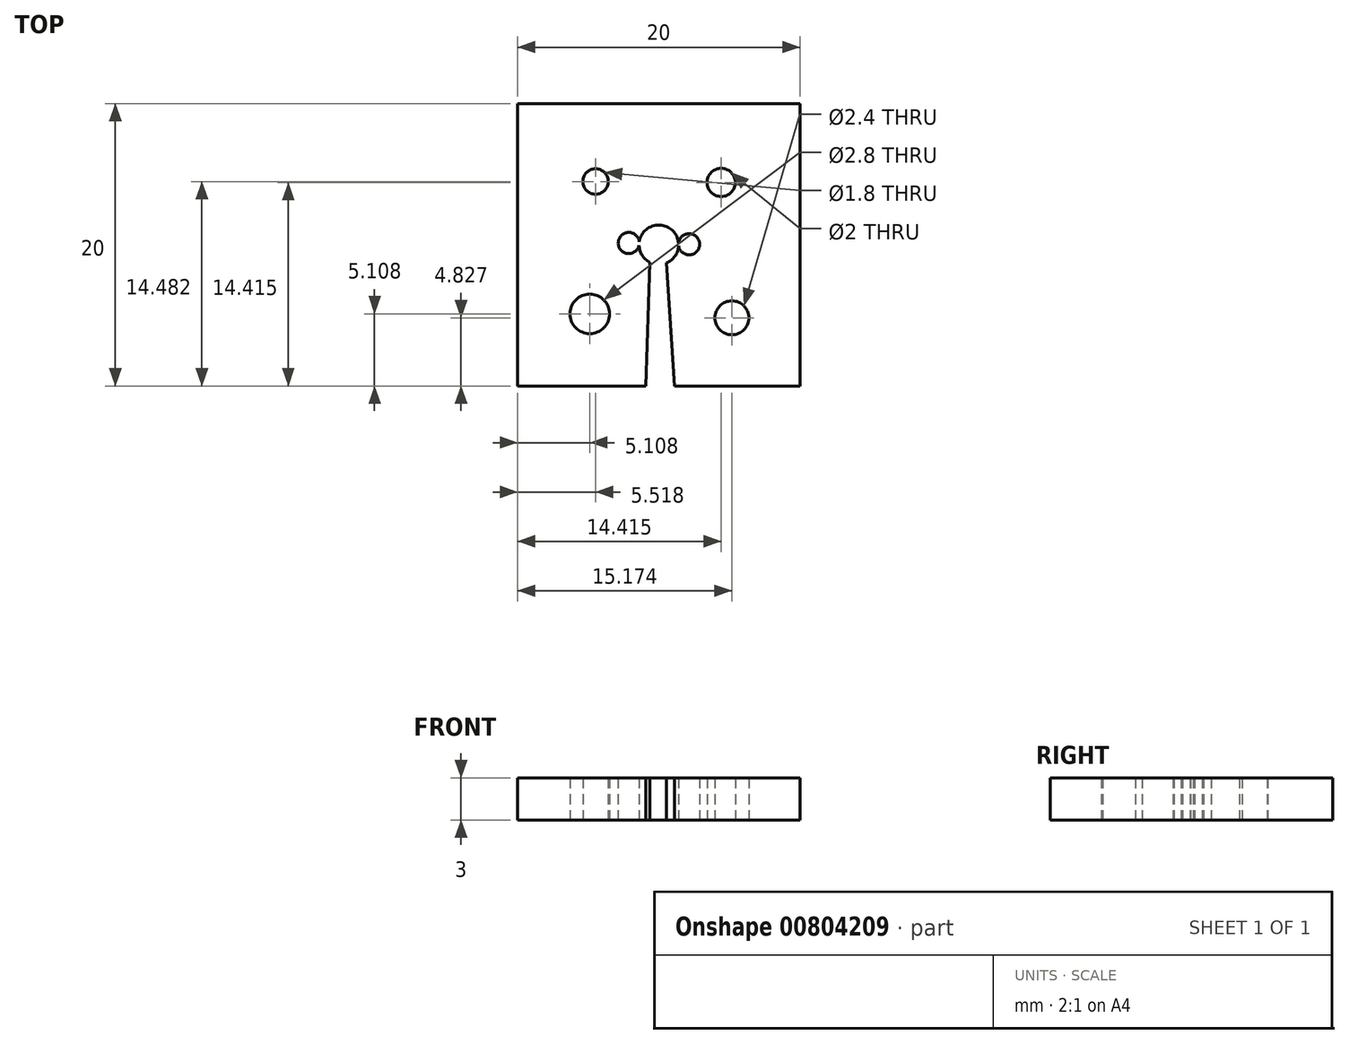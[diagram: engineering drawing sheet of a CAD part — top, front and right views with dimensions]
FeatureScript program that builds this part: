
annotation { "Feature Type Name" : "Feature", "Feature Type Description" : "" }
export const myFeature = defineFeature(function(context is Context, id is Id, definition is map)
    precondition{}
    {
        {
            var Q0;
            Q0=qCreatedBy(makeId("Top.planeOp"),FACE);
            var sketch = newSketch(context, id + "F0", { "sketchPlane" : qUnion([Q0])});
            skLineSegment(sketch, "E0.bottom", {"start": v(0, 0) * mm, "end": v(9.08, 0) * mm});
            skLineSegment(sketch, "E0.top", {"start": v(0, 20) * mm, "end": v(20, 20) * mm});
            skLineSegment(sketch, "E0.left", {"start": v(0, 0) * mm, "end": v(0, 20) * mm});
            skLineSegment(sketch, "E0.right", {"start": v(20, 0) * mm, "end": v(20, 20) * mm});
            skLineSegment(sketch, "E1", {"start": v(0, 20) * mm, "end": v(20, 0) * mm, "construction": true});
            skLineSegment(sketch, "E2", {"start": v(0, 0) * mm, "end": v(20, 20) * mm, "construction": true});
            skCircle(sketch, "E3", {"center": v(14.42, 14.42) * mm, "radius": 1 * mm});
            skCircle(sketch, "E4", {"center": v(5.52, 14.48) * mm, "radius": 0.9 * mm});
            skCircle(sketch, "E5", {"center": v(5.1, 5.1) * mm, "radius": 1.4 * mm});
            skCircle(sketch, "E6", {"center": v(15.17, 4.83) * mm, "radius": 1.2 * mm});
            skArc(sketch, "E7", {"start": v(10.55, 8.71) * mm, "mid": v(10.05, 11.4) * mm, "end": v(9.37, 8.75) * mm});
            skCircle(sketch, "E8", {"center": v(12.14, 10.03) * mm, "radius": 0.75 * mm});
            skPoint(sketch, "E8.first.point", {"position": v(11.4, 10.13) * mm});
            skPoint(sketch, "E8.second.point", {"position": v(12.83, 10.33) * mm});
            skPoint(sketch, "E8.third.point", {"position": v(12.06, 9.29) * mm});
            skCircle(sketch, "E9", {"center": v(7.87, 10.12) * mm, "radius": 0.75 * mm});
            skPoint(sketch, "E9.first.point", {"position": v(8.62, 10.21) * mm});
            skPoint(sketch, "E9.second.point", {"position": v(7.15, 9.91) * mm});
            skPoint(sketch, "E9.third.point", {"position": v(7.58, 10.81) * mm});
            skLineSegment(sketch, "E10", {"start": v(9.08, 0) * mm, "end": v(9.37, 8.75) * mm});
            skLineSegment(sketch, "E11", {"start": v(11.11, 0) * mm, "end": v(10.55, 8.71) * mm});
            skLineSegment(sketch, "E12.trimOffspring", {"start": v(11.11, 0) * mm, "end": v(20, 0) * mm});
            skSolve(sketch);
        }
        {
            var Q0;
            Q0=makeQuery(id+"F0.imprint","IMPRINT",FACE,{"disambiguationData":[TD([[makeQuery(id+"F0.imprint","IMPRINT",EDGE,{"derivedFrom":sQuery(id+"F0.wireOp",EDGE,"E0.bottom")}),1.0]])]});
            extrude(context, id + "F1", {"entities" : qUnion([Q0]), "depth" : 3 * mm, "offsetDistance" : 25 * mm});
        }
    });
